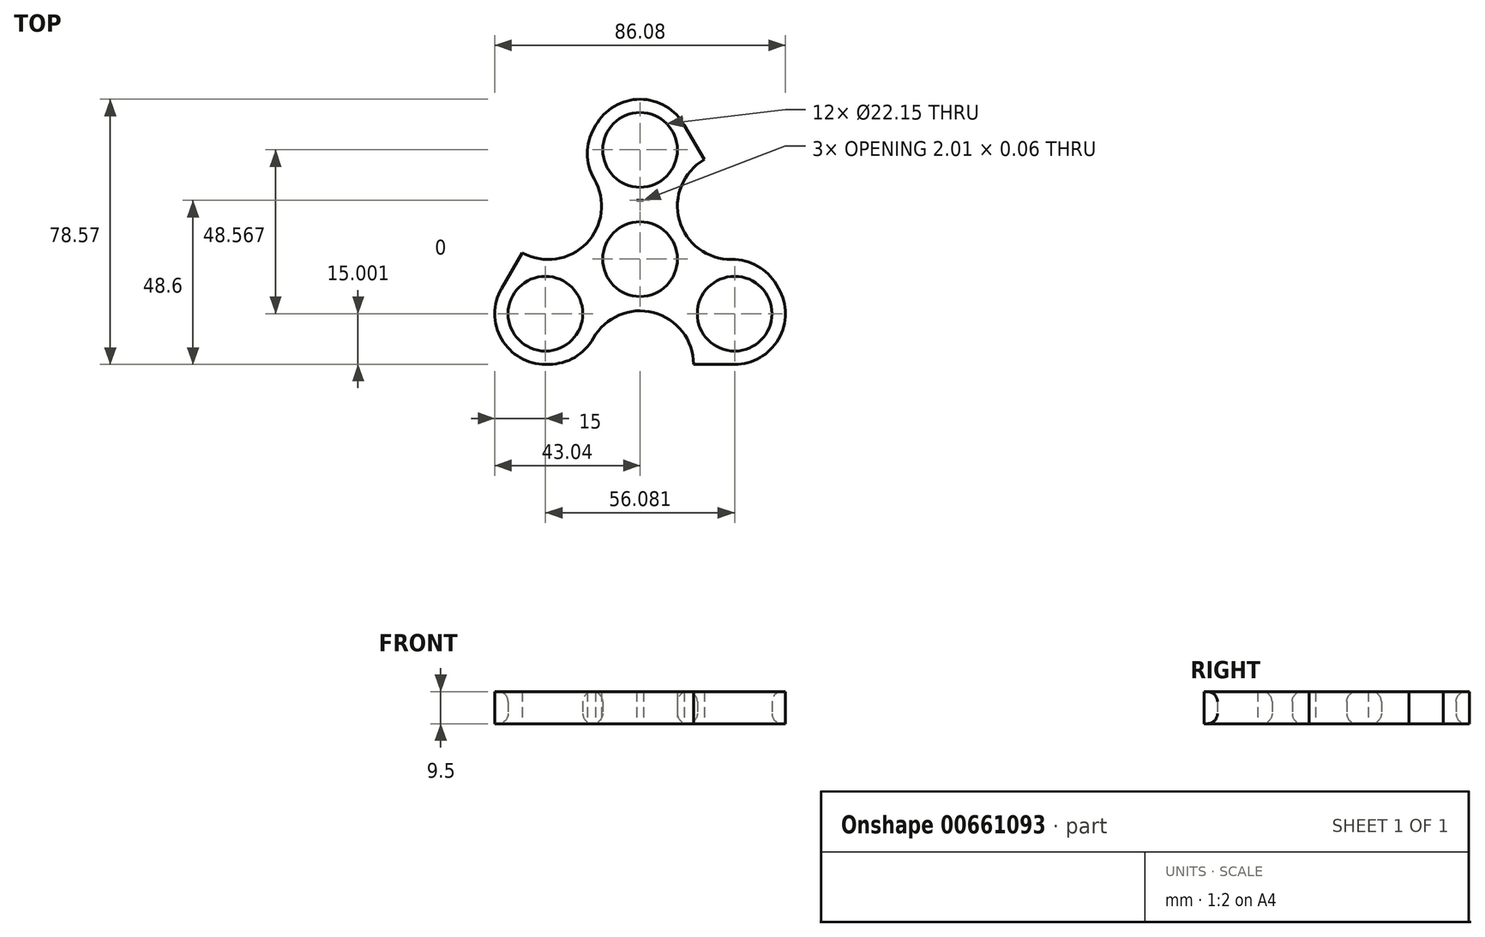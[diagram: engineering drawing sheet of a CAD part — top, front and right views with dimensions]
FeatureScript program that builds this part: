
annotation { "Feature Type Name" : "Feature", "Feature Type Description" : "" }
export const myFeature = defineFeature(function(context is Context, id is Id, definition is map)
    precondition{}
    {
        {
            var Q0;
            Q0=qCreatedBy(makeId("Top.planeOp"),FACE);
            var sketch = newSketch(context, id + "F0", { "sketchPlane" : qUnion([Q0])});
            skCircle(sketch, "E0", {"center": v(0, 0) * mm, "radius": 11.07 * mm});
            skLineSegment(sketch, "E1", {"start": v(0, 47.38) * mm, "end": v(0, 43.45) * mm});
            skCircle(sketch, "E2", {"center": v(0, 32.38) * mm, "radius": 11.07 * mm});
            skCircle(sketch, "E3.1.0", {"center": v(-28.04, -16.19) * mm, "radius": 11.07 * mm});
            skCircle(sketch, "E3.2.0", {"center": v(28.04, -16.19) * mm, "radius": 11.07 * mm});
            skArc(sketch, "E4", {"start": v(-1, 17.41) * mm, "mid": v(0, 17.38) * mm, "end": v(1, 17.41) * mm});
            skArc(sketch, "E5.1.0", {"start": v(-41.03, -8.69) * mm, "mid": v(-41.03, -23.69) * mm, "end": v(-28.04, -31.19) * mm});
            skLineSegment(sketch, "E6", {"start": v(-12.83, 40.15) * mm, "end": v(-19.08, 29.32) * mm});
            skLineSegment(sketch, "E7", {"start": v(-28.04, -31.19) * mm, "end": v(-15.85, -31.19) * mm});
            skLineSegment(sketch, "E8", {"start": v(12.83, 40.15) * mm, "end": v(19, 29.46) * mm});
            skArc(sketch, "E9.trimOffspring", {"start": v(13.14, 39.6) * mm, "mid": v(0, 47.38) * mm, "end": v(-13.14, 39.6) * mm});
            skArc(sketch, "E10.trimOffspring", {"start": v(28.04, -31.19) * mm, "mid": v(41.03, -23.69) * mm, "end": v(41.03, -8.69) * mm});
            skArc(sketch, "E11.trimOffspring", {"start": v(1, 17.41) * mm, "mid": v(0, 17.44) * mm, "end": v(-1, 17.41) * mm});
            skLineSegment(sketch, "E12.trimOffspring", {"start": v(0, 21.3) * mm, "end": v(0, 17.44) * mm});
            skLineSegment(sketch, "E13.trimOffspring", {"start": v(0, 43.45) * mm, "end": v(0, 47.38) * mm});
            skPoint(sketch, "E14.endSnap0", {"position": v(26.93, 15.73) * mm});
            skArc(sketch, "E15", {"start": v(19, 29.46) * mm, "mid": v(13.2, 7.8) * mm, "end": v(34.86, 2) * mm});
            skArc(sketch, "E16", {"start": v(15.85, -31.19) * mm, "mid": v(0, -15.34) * mm, "end": v(-15.85, -31.19) * mm});
            skArc(sketch, "E17", {"start": v(-34.93, 1.87) * mm, "mid": v(-13.52, 7.8) * mm, "end": v(-19.08, 29.32) * mm});
            skLineSegment(sketch, "E18.trimOffspring", {"start": v(-34.93, 1.87) * mm, "end": v(-41.03, -8.69) * mm});
            skLineSegment(sketch, "E19.trimOffspring", {"start": v(15.85, -31.19) * mm, "end": v(28.04, -31.19) * mm});
            skLineSegment(sketch, "E20.trimOffspring", {"start": v(34.86, 2) * mm, "end": v(41.03, -8.69) * mm});
            skPoint(sketch, "E21.orphan", {"position": v(26.93, 15.55) * mm});
            skSolve(sketch);
        }
        {
            var Q0;
            Q0 = qSketchRegion(id + "F0", true);
            extrude(context, id + "F1", {"entities" : qUnion([Q0]), "depth" : 9.5 * mm, "offsetDistance" : 25.4 * mm});
        }
        {
            var Q0;
            Q0=makeQuery(id+"F1.opExtrude","SWEPT_EDGE",EDGE,{"disambiguationData":[OSD([sQuery(id+"F0.wireOp",EDGE,"E15"),sQuery(id+"F0.wireOp",EDGE,"E20.trimOffspring")])]});
            var Q1;
            Q1=makeQuery(id+"F1.opExtrude","SWEPT_EDGE",EDGE,{"disambiguationData":[OSD([sQuery(id+"F0.wireOp",EDGE,"E6"),sQuery(id+"F0.wireOp",EDGE,"E17")])]});
            var Q2;
            Q2=makeQuery(id+"F1.opExtrude","SWEPT_EDGE",EDGE,{"disambiguationData":[OSD([sQuery(id+"F0.wireOp",EDGE,"E7"),sQuery(id+"F0.wireOp",EDGE,"E16")])]});
            fillet(context, id + "F2", {"entities" : qUnion([Q0, Q1, Q2]), "radius" : 15 * mm, "tangentPropagation" : true, "allowEdgeOverflow" : false});
        }
        {
            var Q0;
            Q0=makeQuery(id+"F1.opExtrude","CAP_EDGE",EDGE,{"disambiguationData":[OSD([sQuery(id+"F0.wireOp",EDGE,"E0")])],"isStart":false});
            var Q1;
            Q1=makeQuery(id+"F1.opExtrude","CAP_EDGE",EDGE,{"disambiguationData":[OSD([sQuery(id+"F0.wireOp",EDGE,"E3.1.0")])],"isStart":false});
            var Q2;
            Q2=makeQuery(id+"F1.opExtrude","CAP_EDGE",EDGE,{"disambiguationData":[OSD([sQuery(id+"F0.wireOp",EDGE,"E2")])],"isStart":false});
            var Q3;
            Q3=makeQuery(id+"F1.opExtrude","CAP_EDGE",EDGE,{"disambiguationData":[OSD([sQuery(id+"F0.wireOp",EDGE,"E3.2.0")])],"isStart":false});
            var Q4;
            Q4=makeQuery(id+"F1.opExtrude","CAP_EDGE",EDGE,{"disambiguationData":[OSD([sQuery(id+"F0.wireOp",EDGE,"E2")])],"isStart":true});
            var Q5;
            Q5=makeQuery(id+"F1.opExtrude","CAP_EDGE",EDGE,{"disambiguationData":[OSD([sQuery(id+"F0.wireOp",EDGE,"E3.1.0")])],"isStart":true});
            var Q6;
            Q6=makeQuery(id+"F1.opExtrude","CAP_EDGE",EDGE,{"disambiguationData":[OSD([sQuery(id+"F0.wireOp",EDGE,"E0")])],"isStart":true});
            var Q7;
            Q7=makeQuery(id+"F1.opExtrude","CAP_EDGE",EDGE,{"disambiguationData":[OSD([sQuery(id+"F0.wireOp",EDGE,"E3.2.0")])],"isStart":true});
            fillet(context, id + "F3", {"entities" : qUnion([Q0, Q1, Q2, Q3, Q4, Q5, Q6, Q7]), "radius" : 3 * mm, "tangentPropagation" : true, "allowEdgeOverflow" : false});
        }
    });
